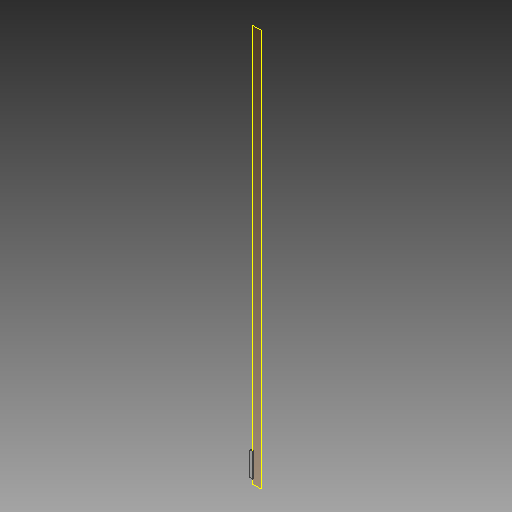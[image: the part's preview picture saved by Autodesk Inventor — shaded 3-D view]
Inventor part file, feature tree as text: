
AUTODESK INVENTOR PART (.ipt)
format: ipt  version: 2018 (Build 220112000, 112)  size: 80,384 bytes
history: native  units: mm
features: other x3, plane x1, extrude x1, sketch x1
ambient origin geometry x8: Origin, YZ Plane, XZ Plane, XY Plane, X Axis, Y Axis, Z Axis, Center Point
bodies: Solid1 (feature_tree)
feature tree (6):
  plane  "Work Plane1"
  extrude  "Extrusion1"  Depth=80.0mm
  sketch  "Sketch1"  dims[d0=10.0mm d1=80.0mm d2=4.0mm d3=0.0mm]
  parser-record x1  (decoder bookkeeping rows leaked as tree rows — omitted from the tree; the rows remain in map.json)
  other  "håndfang.iam"
  other  "stang:2"
note: 1 file-system path scrubbed to <path> (originals preserved in map.json)
